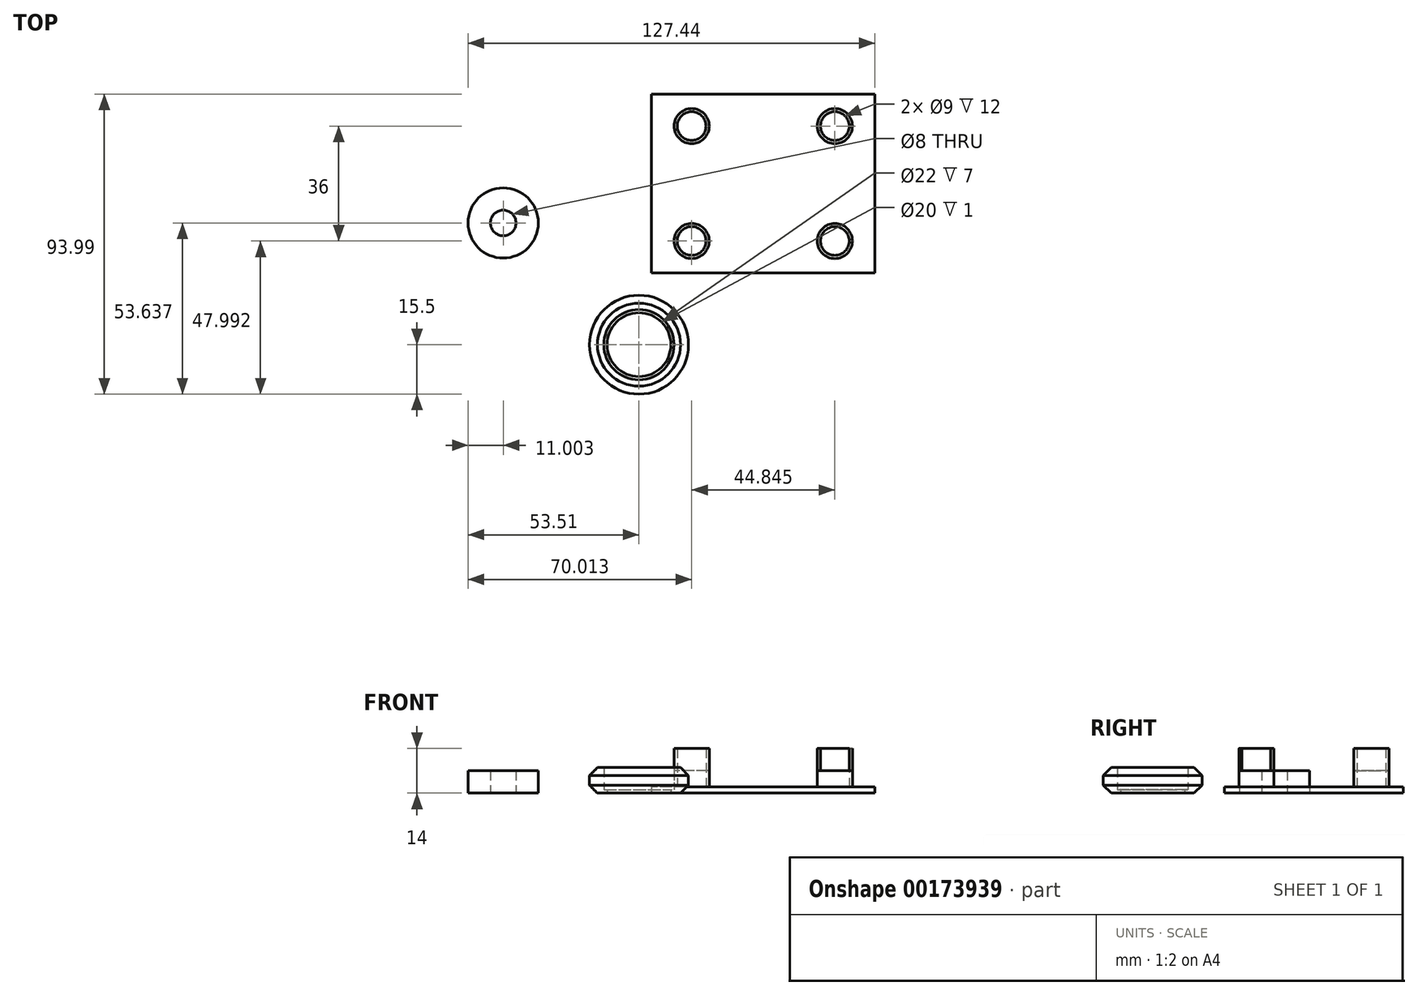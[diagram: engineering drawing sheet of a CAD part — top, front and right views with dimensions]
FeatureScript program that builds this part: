
annotation { "Feature Type Name" : "Feature", "Feature Type Description" : "" }
export const myFeature = defineFeature(function(context is Context, id is Id, definition is map)
    precondition{}
    {
        {
            var Q0;
            Q0=qCreatedBy(makeId("Right.planeOp"),FACE);
            var sketch = newSketch(context, id + "F0", { "sketchPlane" : qUnion([Q0])});
            skLineSegment(sketch, "E0", {"start": v(0, 0) * mm, "end": v(2, 0) * mm});
            skLineSegment(sketch, "E1", {"start": v(2, 0) * mm, "end": v(6, 4) * mm});
            skLineSegment(sketch, "E2", {"start": v(6, 4) * mm, "end": v(2, 8) * mm});
            skLineSegment(sketch, "E3", {"start": v(2, 8) * mm, "end": v(0, 8) * mm});
            skLineSegment(sketch, "E4", {"start": v(0, 8) * mm, "end": v(0, 0) * mm});
            skLineSegment(sketch, "E5", {"start": v(-11, 0) * mm, "end": v(-11, 5.99) * mm});
            skLineSegment(sketch, "E6.bottom", {"start": v(0, 1) * mm, "end": v(-1, 1) * mm});
            skLineSegment(sketch, "E6.top", {"start": v(0, 0) * mm, "end": v(-1, 0) * mm});
            skLineSegment(sketch, "E6.left", {"start": v(0, 1) * mm, "end": v(0, 0) * mm});
            skLineSegment(sketch, "E6.right", {"start": v(-1, 1) * mm, "end": v(-1, 0) * mm});
            skLineSegment(sketch, "E7", {"start": v(4.5, 5.5) * mm, "end": v(4.5, 2.5) * mm});
            skSolve(sketch);
        }
        {
            var Q0;
            {var subQ4=sQuery(id+"F0.wireOp",EDGE,"E0");Q0=makeQuery(id+"F0.imprint","IMPRINT",FACE,{"disambiguationData":[TD([[makeQuery(id+"F0.imprint","IMPRINT",EDGE,{"derivedFrom":subQ4}),1.0]])]});}
            var Q1;
            Q1=makeQuery(id+"F0.imprint","IMPRINT",FACE,{"disambiguationData":[TD([[makeQuery(id+"F0.imprint","IMPRINT",EDGE,{"derivedFrom":sQuery(id+"F0.wireOp",EDGE,"E6.bottom")}),1.0]])]});
            var Q2;
            Q2=sQuery(id+"F0.wireOp",EDGE,"E5");
            revolve(context, id + "F1", {"entities" : qUnion([Q0, Q1]), "axis" : qUnion([Q2]), "revolveType" : RevolveType.FULL});
        }
        {
            var Q0;
            Q0=qCreatedBy(makeId("Top.planeOp"),FACE);
            var sketch = newSketch(context, id + "F2", { "sketchPlane" : qUnion([Q0])});
            skCircle(sketch, "E8", {"center": v(-42.5, 27.14) * mm, "radius": 11 * mm});
            skCircle(sketch, "E9", {"center": v(-42.5, 27.14) * mm, "radius": 4 * mm});
            skSolve(sketch);
        }
        {
            var Q0;
            Q0 = qSketchRegion(id + "F2", true);
            extrude(context, id + "F3", {"entities" : qUnion([Q0]), "depth" : 7 * mm});
        }
        {
            var Q0;
            Q0=qCreatedBy(makeId("Top.planeOp"),FACE);
            var sketch = newSketch(context, id + "F4", { "sketchPlane" : qUnion([Q0])});
            skLineSegment(sketch, "E10.bottom", {"start": v(73.93, 11.5) * mm, "end": v(3.93, 11.5) * mm});
            skLineSegment(sketch, "E10.top", {"start": v(73.93, 67.5) * mm, "end": v(3.93, 67.5) * mm});
            skLineSegment(sketch, "E10.left", {"start": v(73.93, 11.5) * mm, "end": v(73.93, 67.5) * mm});
            skLineSegment(sketch, "E10.right", {"start": v(3.93, 11.5) * mm, "end": v(3.93, 67.5) * mm});
            skSolve(sketch);
        }
        {
            var Q0;
            Q0 = qSketchRegion(id + "F4", true);
            extrude(context, id + "F5", {"entities" : qUnion([Q0]), "depth" : 2 * mm});
        }
        {
            var Q0;
            Q0=makeQuery(id+"F5.opExtrude","CAP_FACE",FACE,{"disambiguationData":[OSD([sQuery(id+"F4.wireOp",EDGE,"E10.bottom"),sQuery(id+"F4.wireOp",EDGE,"E10.top"),sQuery(id+"F4.wireOp",EDGE,"E10.left"),sQuery(id+"F4.wireOp",EDGE,"E10.right")])],"isStart":false});
            var sketch = newSketch(context, id + "F6", { "sketchPlane" : qUnion([Q0])});
            skLineSegment(sketch, "E11", {"start": v(38.93, 11.5) * mm, "end": v(38.93, 67.5) * mm});
            skLineSegment(sketch, "E12", {"start": v(3.93, 39.5) * mm, "end": v(73.93, 39.5) * mm});
            skCircle(sketch, "E13", {"center": v(61.35, 21.5) * mm, "radius": 5.5 * mm});
            skCircle(sketch, "E14", {"center": v(61.35, 21.5) * mm, "radius": 4.5 * mm});
            skCircle(sketch, "E15.MirrorC", {"center": v(16.5, 21.5) * mm, "radius": 5.5 * mm});
            skCircle(sketch, "E16.MirrorC", {"center": v(16.5, 21.5) * mm, "radius": 4.5 * mm});
            skLineSegment(sketch, "E17.MirrorCS", {"start": v(73.93, 39.5) * mm, "end": v(3.93, 39.5) * mm});
            skCircle(sketch, "E18.MirrorC", {"center": v(61.35, 57.5) * mm, "radius": 4.5 * mm});
            skCircle(sketch, "E19.MirrorC", {"center": v(61.35, 57.5) * mm, "radius": 5.5 * mm});
            skCircle(sketch, "E20.MirrorC", {"center": v(16.5, 57.5) * mm, "radius": 5.5 * mm});
            skCircle(sketch, "E21.MirrorC", {"center": v(16.5, 57.5) * mm, "radius": 4.5 * mm});
            skSolve(sketch);
        }
        {
            var Q0;
            Q0=makeQuery(id+"F6.imprint","IMPRINT",FACE,{"disambiguationData":[TD([[makeQuery(id+"F6.imprint","IMPRINT",EDGE,{"derivedFrom":sQuery(id+"F6.wireOp",EDGE,"E14")}),1.0]])]});
            var Q1;
            Q1=makeQuery(id+"F6.imprint","IMPRINT",FACE,{"disambiguationData":[TD([[makeQuery(id+"F6.imprint","IMPRINT",EDGE,{"derivedFrom":sQuery(id+"F6.wireOp",EDGE,"E16.MirrorC")}),-1.0]])]});
            var Q2;
            Q2=makeQuery(id+"F6.imprint","IMPRINT",FACE,{"disambiguationData":[TD([[makeQuery(id+"F6.imprint","IMPRINT",EDGE,{"derivedFrom":sQuery(id+"F6.wireOp",EDGE,"E21.MirrorC")}),1.0]])]});
            var Q3;
            Q3=makeQuery(id+"F6.imprint","IMPRINT",FACE,{"disambiguationData":[TD([[makeQuery(id+"F6.imprint","IMPRINT",EDGE,{"derivedFrom":sQuery(id+"F6.wireOp",EDGE,"E18.MirrorC")}),-1.0]])]});
            extrude(context, id + "F7", {"entities" : qUnion([Q0, Q1, Q2, Q3]), "operationType" : NewBodyOperationType.ADD, "depth" : 12 * mm});
        }
        {
            var Q0;
            Q0 = qSketchRegion(id + "F6", true);
            extrude(context, id + "F8", {"entities" : qUnion([Q0]), "operationType" : NewBodyOperationType.ADD, "depth" : 5 * mm});
        }
    });
